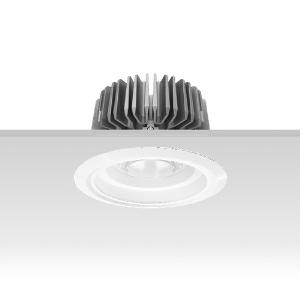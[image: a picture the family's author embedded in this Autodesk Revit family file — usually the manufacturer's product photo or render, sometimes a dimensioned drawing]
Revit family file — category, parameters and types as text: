
# Revit family: 3f_filippi_-_3f_reno_bianco_ampio_3f_filippi_-_30379_a01023_-_3f_reno_150_wh_2000-930_dali_wide___vt_wh_690c
name_source: partatom
category: Lighting Fixtures
units: mm (PartAtom-declared; Revit-internal decimal feet)

## family parameters
Cut with Voids When Loaded = No
Host = Face
Light Source = No
Part Type = Normal
Room Calculation Point = No
Round Connector Dimension = Use Diameter
Shared = No

## types (1)
- 3F Filippi - 3F Reno Bianco Ampio (1 x LED, 1888 lm, 24 W, 3000 K)
    Apparent Load = 24 VA
    Approval mark = CE
    CIE Flux Codes = 74 93 99 100 100
    Color Rendering = 90
    Color Temperature = 3000 K
    Control Gear = Electronic transformer
    Default Elevation = 1800 mm
    Description = ILLUMINOTECHNICAL
Luminous efficiency 100% (DLOR 100%, ULOR 0%).
Initial luminous flux of the luminaire 1888 lm.
Direct symmetric wide distribution.
Installation Interdistance Transv.D = 1.54 x hu - Long.D = 1.54 x hu.
Tabular UGR (CIE 117 - 4H-8H; S=0.25H; 70/50/20): RUG 23.2 - 23.
Beam angle: 74° - 73°.
Luminous efficacy 79 lm/W.
Lifetime (L90/B10): 30000 h. (tq+25°C)
Lifetime (L85/B10): 50000 h. (tq+25°C)
Lifetime (L70/B10): 80000 h. (tq+25°C)
Sudden decreased luminous flux after 50000 hours: 0% (C0).
Photobiological safety in compliance with IEC/TR 62778: RG0 risk exempt, (IEC 62471).
In compliance with IEC/EN 62722-2-1 - IEC/EN 62717 standards.

SOURCE
Compact LED module 2000/930.
Energy efficiency class (UE 2019/2020 - UE 2019/2015): E.
CIE 13.3 Colour rendering index: CRI >90 (R9 >50%).
IES TM-30 Fidelity Index: Rf = 92 Rg = 101.
CCT nominal colour temperature 3000 K.
Colour initial tolerance (MacAdam): SDCM 3.
Zhaga Book 3 compliant.

MECHANICAL
Passive heat dissipator in die-casting aluminium, oversized, for optimum thermal management of the LED module.
Parabolic element with graduated/concentric rings in white polycarbonate.
Transparent external lens with glossy and satin differentiated surfaces, with a cooling and anti-insect system in methacrylate (PMMA).
Fastening spring clips in stainless steel.
Dimensions: diameter 176 mm, height 111 mm. Weight 0.85 kg.
IP44 protection degree for exposed part, IP20 for recessed part.
Mechanical strength to impacts IK06 (1 joule).
Glow-wire test resistance 650°C.

ELECTRICAL
Wiring on a separate unit.
Halogen Free DALI-2 DATI (Parts 251, 252, 253), PUSH-DIM, electronic wiring 230V-50/60Hz, power factor 0.95 at full load, THD <25%, constant output current, SELV, class II, 1 driver, 1 DALI addresse.
Power of the luminaire 24 W.
ENEC - CE.
SAFE FLICKER: PstLM=<1 and SVM=<0.4 (IEC TR 61547-1 and IEC TR 63158), to ensure a more comfortable and safe light.
Luminaire compliant with EN 60598-2-22 for power supply from a centralised emergency system CPSS (Central Power Supply System), not incorporated in the luminaire - high risk areas excluded. The default power and flux are 100% in AC and 100% in DC.
Ambient temperature from 0°C to +25°C.
Temperature class T6 max 85°C.
Relative humidity UR: <85%.

INSTALLATION
Pull-up recessed fitting.
False ceiling carving: 150 mm.
All accessories dedicated to this product are available on the Catalog and on our website www.3F-Filippi.com.

ACCESSORIES
A01023 - VT transparent glass, tempered, not flammable, locked and in line with the trim, in white polycarbonate.

APPLICATIONS
Environments: architectural, commercial, exhibition areas, transit areas, corridors, shops, display windows, service areas.
In false ceilings with narrow voids.

LIGHT MANAGEMENT
Recommended minimum setting: 10%.
The luminaire, equipped with (DALI-2 DATI) driver, can be controlled manually with 3F Easy Dim technology or automatically/manually with wired or wireless DALI/D2D control systems.
The D2D driver guarantees interoperability with other devices with the same certification by making the following information available:
Device Data (Part 251), Energy Report (Part 252), Diagnosis & Maintenance (Part 253).
In electrical systems without a regulation system (manual or automatic) and DALI bus, a suitable jumper must be made on the DA-DA terminals of the appliance.

WARNING
Luminaire designed for disposal/recycling at end-of-life.
Replaceable (LED only) light source by a professional. Replaceable control gear by a professional.
    Height = 0 mm  [stored 0 ft]
    Lamp = 1 x LED
    Lamp Light Flux = 1888 lm
    Lamp Power = 24 W
    Lamp count = 1
    Length = 176 mm
    Lifetime = 50000 h
    Luminous efficacy = 79 lm/W
    Manufacturer = 3F Filippi
    ModVariant = No
    Model = 3F Filippi - 30379+A01023 - 3F Reno 150 WH 2000-930 DALI WIDE + VT WH
    Mounting Place = Ceiling
    Mounting Type = Recessed
    Number of Poles = 1
    OnlyDefault = Yes
    Power Factor = 1
    Product Name = 3F Filippi - 3F Reno Bianco Ampio
    Product group = recessed luminaire
    ProductGroupID = 4
    Protection Class = Protection class II
    Protection Degree = IP 20
    RLX_Detail_Level = 1
    RLX_Emergency_Light_Flux = 0 lm
    RLX_Emergency_Type = 0
    RLX_Emergency_Type_DB = No
    RlxData = <blob elided: 86817 chars, md5=56203e41>
    Socket = socket
    Standby Power = 0 W
    System Light Flux = 1888 lm
    System Power = 24 W
    Type Comments = Product without accessories
    Type Image = 3ffilippi_3f_reno_150_wh_d150__a01023.jpg
    URL = http://relux.com
    VarID = ---
    Voltage = 0 V
    Weight = 0.00 kg
    Width = 0 mm  [stored 0 ft]

note: [stored X ft] marks values corroborated as IEEE doubles in the binary element streams (Revit-internal decimal feet)

## geometry (parser evidence)
native form markers: Blend x4, Sweep x14
no freeform markers — native parametric forms only
